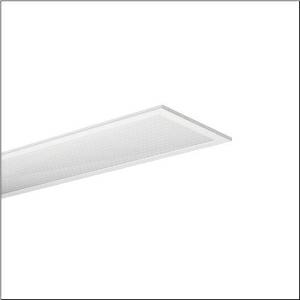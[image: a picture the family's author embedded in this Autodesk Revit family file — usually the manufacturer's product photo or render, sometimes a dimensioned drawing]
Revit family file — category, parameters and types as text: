
# Revit family: apollon_21_linear_51mq14wm2414
name_source: partatom
category: Lighting Fixtures
units: mm (PartAtom-declared; Revit-internal decimal feet)

## family parameters
Cut with Voids When Loaded = No
Host = Face
Light Source = No
Part Type = Normal
Room Calculation Point = No
Round Connector Dimension = Use Diameter
Shared = No

## types (1)
- --- (1 x LED, 5060 lm, 29.3 W, 4000K)
    Apparent Load = 29 VA
    CIE Flux Codes = 60 87 97 100 100
    Color Rendering = 80
    Color Temperature = 4000K
    Default Elevation = 1800 mm
    Description = Apollon 21 linear, office luminaire, primary optical cover: micro prismatic cover, of PMMA, CAT 2 (L<= 3000cd/m²), light emission: direct distribution, primary light characteristic: symmetric, installation type: lay-in mounting, recessed, LED, rated luminous flux: 4.390lm, luminous efficacy: 174lm/W, light colour: 840, colour temperature: 4000K, control gear: ON/OFF Multilumen, with terminal, 3-pole, mains connection: 220..240V, AC/DC, 0/50..60Hz, rated input power: 25.3W, suitable for self-contained emergency lighting element 59MQE002602A with integrated self-test function according to EN 60598-2-22, housing, of aluminium, coated, traffic white (RAL 9016), module: M625, length: 1.245mm, width: 307mm, height: 55mm, housing upper side, of sheet steel, galvanised, protection rating (complete): IP20, protection rating (lamp compartment, on room side): IP50, insulation class (complete): insulation class II (safety insulation), certification: CE, ENEC, UKCA, impact resistance: IK03, permissible operating ambient temperature: -20..+45°C, standard: EN 60598-2-22, corresponds to IFS (International Featured Standards) requirements for safety and quality in the food industry, packaging unit: 1 piece
    Height = 0 mm  [stored 0 ft]
    Lamp = 1 x LED
    Lamp Light Flux = 5060 lm
    Lamp Power = 29.3 W
    Lamp count = 1
    Length = 1245 mm
    Luminous efficacy = 173 lm/W
    Manufacturer = Siteco
    ModVariant = No
    Model = 51MQ14WM2414
    Mounting Place = Ceiling
    Mounting Type = Recessed
    Number of Poles = 1
    OnlyDefault = Yes
    Power Factor = 1
    Product Name = Apollon 21 linear
    Product group = office luminaire | ceiling recessed
    ProductGroupID = 400
    Protection Class = Protection class II
    Protection Degree = IP 20
    RLX_Detail_Level = 1
    RLX_Emergency_Light_Flux = 0 lm
    RLX_Emergency_Type = 0
    RLX_Emergency_Type_DB = No
    RlxData = <blob elided: 16905 chars, md5=96efa549>
    Socket = socket
    Standby Power = 0 W
    System Light Flux = 5060 lm
    System Power = 29 W
    Type Comments = factory setting: luminous flux: 100 % | (ON | ON | ON) | 700 mA
    Type Image = l_1291045.jpg
    URL = http://relux.com
    VarID = @adj_075885
    Voltage = 0 V
    Weight = 0.00 kg
    Width = 307 mm

note: [stored X ft] marks values corroborated as IEEE doubles in the binary element streams (Revit-internal decimal feet)

## geometry (parser evidence)
native form markers: Blend x4, Sweep x12
no freeform markers — native parametric forms only
